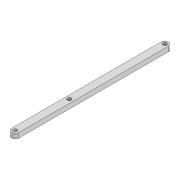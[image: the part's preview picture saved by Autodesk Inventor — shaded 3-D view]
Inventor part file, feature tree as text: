
AUTODESK INVENTOR PART (.ipt)
format: ipt  version: 2022 (Build 260153000, 153)  size: 89,600 bytes
history: native  units: mm
features: extrude x1, sketch x1
ambient origin geometry x8: Origin, YZ Plane, XZ Plane, XY Plane, X Axis, Y Axis, Z Axis, Center Point
bodies: Solid1 (feature_tree)
feature tree (2):
  extrude  "Extrusion1"  Depth=4.0mm
  sketch  "Sketch1"  dims[d0=3.2mm d1=3.2mm d2=6.0mm d3=122.139mm d4=3.2mm d5=44.122mm d6=4.0mm d7=0.0mm]
